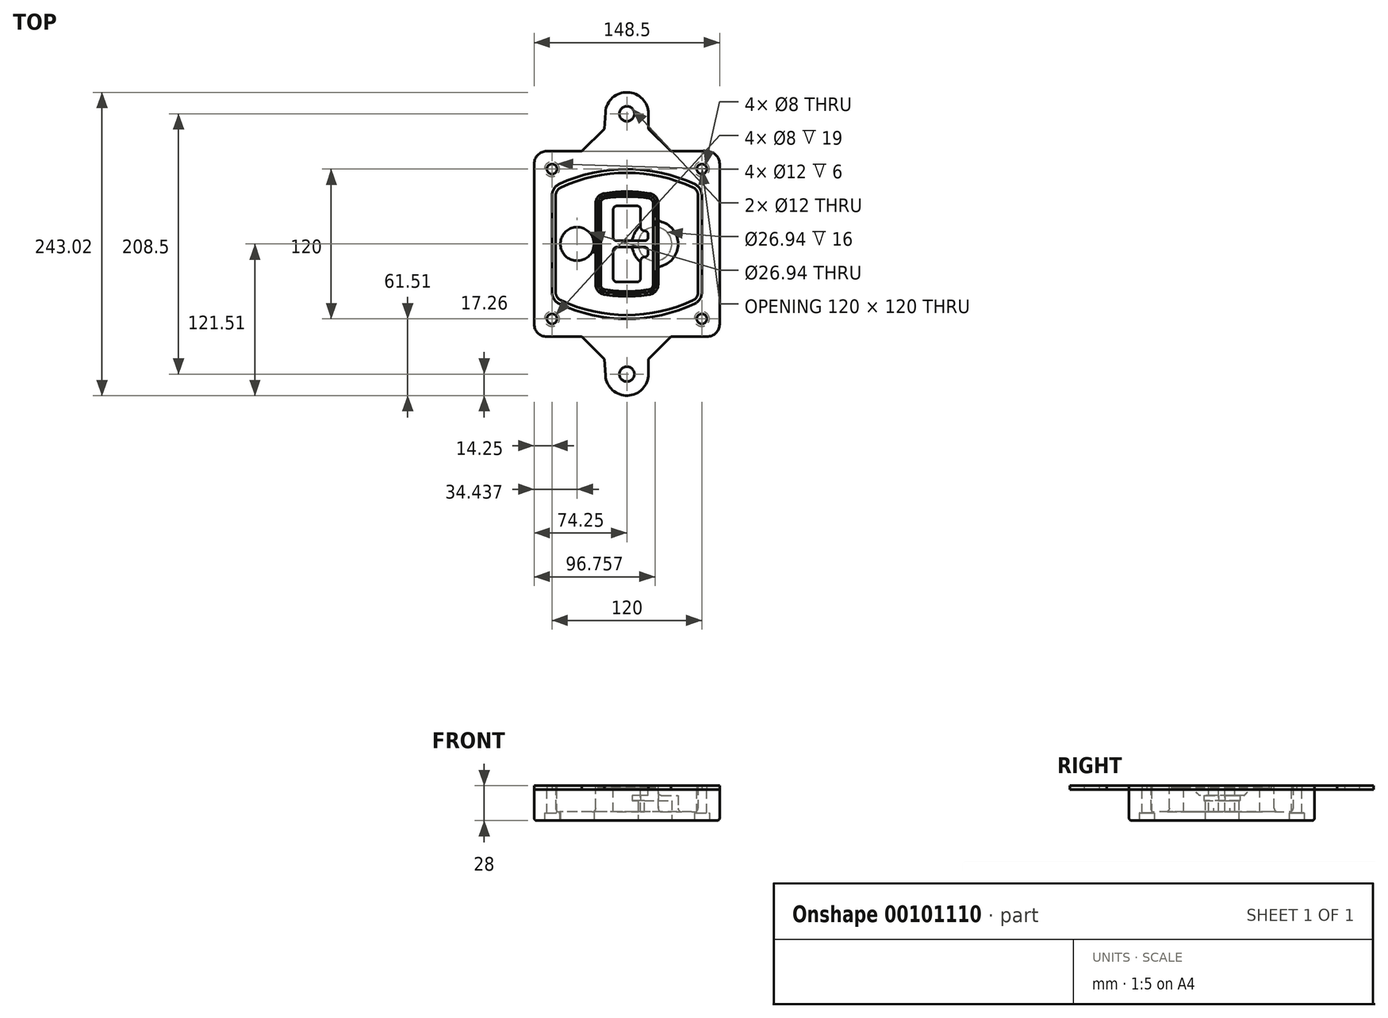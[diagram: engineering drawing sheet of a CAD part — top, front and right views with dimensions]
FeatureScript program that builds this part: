
annotation { "Feature Type Name" : "Feature", "Feature Type Description" : "" }
export const myFeature = defineFeature(function(context is Context, id is Id, definition is map)
    precondition{}
    {
        {
            var Q0;
            Q0=qCreatedBy(makeId("Top.planeOp"),FACE);
            var sketch = newSketch(context, id + "F0", { "sketchPlane" : qUnion([Q0])});
            skPoint(sketch, "E0.rect.middle", {"position": v(0, 0) * mm});
            skLineSegment(sketch, "E1.bottom", {"start": v(-64.25, -74.25) * mm, "end": v(64.25, -74.25) * mm});
            skLineSegment(sketch, "E1.top", {"start": v(-64.25, 74.25) * mm, "end": v(64.25, 74.25) * mm});
            skLineSegment(sketch, "E1.left", {"start": v(-74.25, -64.25) * mm, "end": v(-74.25, 64.25) * mm});
            skLineSegment(sketch, "E1.right", {"start": v(74.25, -64.25) * mm, "end": v(74.25, 64.25) * mm});
            skLineSegment(sketch, "E2", {"start": v(-74.25, 74.25) * mm, "end": v(74.25, -74.25) * mm, "construction": true});
            skLineSegment(sketch, "E3", {"start": v(74.25, 74.25) * mm, "end": v(-74.25, -74.25) * mm, "construction": true});
            skCircle(sketch, "E4", {"center": v(-60, 60) * mm, "radius": 4 * mm});
            skCircle(sketch, "E5", {"center": v(60, 60) * mm, "radius": 4 * mm});
            skCircle(sketch, "E6", {"center": v(60, -60) * mm, "radius": 4 * mm});
            skCircle(sketch, "E7", {"center": v(-60, -60) * mm, "radius": 4 * mm});
            skLineSegment(sketch, "E8", {"start": v(-60, 60) * mm, "end": v(60, 60) * mm, "construction": true});
            skLineSegment(sketch, "E9", {"start": v(60, 60) * mm, "end": v(60, -60) * mm, "construction": true});
            skLineSegment(sketch, "E10", {"start": v(60, -60) * mm, "end": v(-60, -60) * mm, "construction": true});
            skLineSegment(sketch, "E11", {"start": v(-60, -60) * mm, "end": v(-60, 60) * mm, "construction": true});
            skLineSegment(sketch, "E12", {"start": v(-60, 38.83) * mm, "end": v(-60, -38.83) * mm});
            skLineSegment(sketch, "E13", {"start": v(60, 38.83) * mm, "end": v(60, -38.83) * mm});
            skArc(sketch, "E14", {"start": v(54.26, 47.88) * mm, "mid": v(0, 60) * mm, "end": v(-54.26, 47.88) * mm});
            skArc(sketch, "E15", {"start": v(-54.26, -47.88) * mm, "mid": v(0, -60) * mm, "end": v(54.26, -47.88) * mm});
            skLineSegment(sketch, "E16", {"start": v(-60, 0) * mm, "end": v(60, 0) * mm, "construction": true});
            skPoint(sketch, "E17.visualSharp", {"position": v(-60, -45) * mm});
            skArc(sketch, "E17.filletArc", {"start": v(-60, -38.83) * mm, "mid": v(-58.44, -44.2) * mm, "end": v(-54.26, -47.88) * mm});
            skPoint(sketch, "E18.visualSharp", {"position": v(-60, 45) * mm});
            skArc(sketch, "E18.filletArc", {"start": v(-54.26, 47.88) * mm, "mid": v(-58.44, 44.2) * mm, "end": v(-60, 38.83) * mm});
            skPoint(sketch, "E19.visualSharp", {"position": v(60, 45) * mm});
            skArc(sketch, "E19.filletArc", {"start": v(60, 38.83) * mm, "mid": v(58.44, 44.2) * mm, "end": v(54.26, 47.88) * mm});
            skPoint(sketch, "E20.visualSharp", {"position": v(60, -45) * mm});
            skArc(sketch, "E20.filletArc", {"start": v(54.26, -47.88) * mm, "mid": v(58.44, -44.2) * mm, "end": v(60, -38.83) * mm});
            skPoint(sketch, "E21.visualSharp", {"position": v(-74.25, 74.25) * mm});
            skArc(sketch, "E21.filletArc", {"start": v(-64.25, 74.25) * mm, "mid": v(-71.32, 71.32) * mm, "end": v(-74.25, 64.25) * mm});
            skPoint(sketch, "E22.visualSharp", {"position": v(74.25, 74.25) * mm});
            skArc(sketch, "E22.filletArc", {"start": v(74.25, 64.25) * mm, "mid": v(71.32, 71.32) * mm, "end": v(64.25, 74.25) * mm});
            skPoint(sketch, "E23.visualSharp", {"position": v(74.25, -74.25) * mm});
            skArc(sketch, "E23.filletArc", {"start": v(64.25, -74.25) * mm, "mid": v(71.32, -71.32) * mm, "end": v(74.25, -64.25) * mm});
            skPoint(sketch, "E24.visualSharp", {"position": v(-74.25, -74.25) * mm});
            skArc(sketch, "E24.filletArc", {"start": v(-74.25, -64.25) * mm, "mid": v(-71.32, -71.32) * mm, "end": v(-64.25, -74.25) * mm});
            skArc(sketch, "E25.0", {"start": v(57, 38.83) * mm, "mid": v(55.9, 42.58) * mm, "end": v(52.98, 45.17) * mm});
            skLineSegment(sketch, "E25.1", {"start": v(57, 38.83) * mm, "end": v(57, -38.83) * mm});
            skArc(sketch, "E25.2", {"start": v(52.98, -45.17) * mm, "mid": v(55.9, -42.58) * mm, "end": v(57, -38.83) * mm});
            skArc(sketch, "E25.3", {"start": v(-52.98, -45.17) * mm, "mid": v(0, -57) * mm, "end": v(52.98, -45.17) * mm});
            skArc(sketch, "E25.4", {"start": v(-57, -38.83) * mm, "mid": v(-55.9, -42.58) * mm, "end": v(-52.98, -45.17) * mm});
            skArc(sketch, "E25.5", {"start": v(52.98, 45.17) * mm, "mid": v(0, 57) * mm, "end": v(-52.98, 45.17) * mm});
            skLineSegment(sketch, "E25.6", {"start": v(-57, 38.83) * mm, "end": v(-57, -38.83) * mm});
            skArc(sketch, "E25.7", {"start": v(-52.98, 45.17) * mm, "mid": v(-55.9, 42.58) * mm, "end": v(-57, 38.83) * mm});
            skArc(sketch, "E26.0", {"start": v(-55.96, 51.5) * mm, "mid": v(-61.82, 46.33) * mm, "end": v(-64, 38.83) * mm});
            skArc(sketch, "E26.1", {"start": v(55.96, 51.5) * mm, "mid": v(0, 64) * mm, "end": v(-55.96, 51.5) * mm});
            skArc(sketch, "E26.2", {"start": v(64, 38.83) * mm, "mid": v(61.82, 46.33) * mm, "end": v(55.96, 51.5) * mm});
            skLineSegment(sketch, "E26.3", {"start": v(64, 38.83) * mm, "end": v(64, -38.83) * mm});
            skArc(sketch, "E26.4", {"start": v(55.96, -51.5) * mm, "mid": v(61.82, -46.33) * mm, "end": v(64, -38.83) * mm});
            skLineSegment(sketch, "E26.5", {"start": v(-64, 38.83) * mm, "end": v(-64, -38.83) * mm});
            skArc(sketch, "E26.6", {"start": v(-55.96, -51.5) * mm, "mid": v(0, -64) * mm, "end": v(55.96, -51.5) * mm});
            skArc(sketch, "E26.7", {"start": v(-64, -38.83) * mm, "mid": v(-61.82, -46.33) * mm, "end": v(-55.96, -51.5) * mm});
            skSolve(sketch);
        }
        {
            var Q0;
            Q0=makeQuery(id+"F0.imprint","IMPRINT",FACE,{"disambiguationData":[TD([[makeQuery(id+"F0.imprint","IMPRINT",EDGE,{"derivedFrom":sQuery(id+"F0.wireOp",EDGE,"E1.bottom")}),1.0]])]});
            var Q1;
            Q1=makeQuery(id+"F0.imprint","IMPRINT",FACE,{"disambiguationData":[TD([[makeQuery(id+"F0.imprint","IMPRINT",EDGE,{"derivedFrom":sQuery(id+"F0.wireOp",EDGE,"E12")}),1.0]])]});
            var Q2;
            Q2=makeQuery(id+"F0.imprint","IMPRINT",FACE,{"disambiguationData":[TD([[makeQuery(id+"F0.imprint","IMPRINT",EDGE,{"derivedFrom":sQuery(id+"F0.wireOp",EDGE,"E25.0")}),1.0]])]});
            var Q3;
            Q3=makeQuery(id+"F0.imprint","IMPRINT",FACE,{"disambiguationData":[TD([[makeQuery(id+"F0.imprint","IMPRINT",EDGE,{"derivedFrom":sQuery(id+"F0.wireOp",EDGE,"E12")}),-1.0]])]});
            extrude(context, id + "F1", {"entities" : qUnion([Q0, Q1, Q2, Q3]), "oppositeDirection" : true, "depth" : 25 * mm});
        }
        {
            var Q0;
            Q0=makeQuery(id+"F0.imprint","IMPRINT",FACE,{"disambiguationData":[TD([[makeQuery(id+"F0.imprint","IMPRINT",EDGE,{"derivedFrom":sQuery(id+"F0.wireOp",EDGE,"E12")}),1.0]])]});
            extrude(context, id + "F2", {"entities" : qUnion([Q0]), "operationType" : NewBodyOperationType.ADD, "depth" : 3 * mm});
        }
        {
            var Q0;
            Q0=makeQuery(id+"F0.imprint","IMPRINT",FACE,{"disambiguationData":[TD([[makeQuery(id+"F0.imprint","IMPRINT",EDGE,{"derivedFrom":sQuery(id+"F0.wireOp",EDGE,"E25.0")}),1.0]])]});
            extrude(context, id + "F3", {"entities" : qUnion([Q0]), "operationType" : NewBodyOperationType.REMOVE, "oppositeDirection" : true, "depth" : 18 * mm});
        }
        {
            var Q0;
            Q0=makeQuery(id+"F2.opExtrude","CAP_FACE",FACE,{"disambiguationData":[OSD([sQuery(id+"F0.wireOp",EDGE,"E12"),sQuery(id+"F0.wireOp",EDGE,"E13"),sQuery(id+"F0.wireOp",EDGE,"E14"),sQuery(id+"F0.wireOp",EDGE,"E15"),sQuery(id+"F0.wireOp",EDGE,"E17.filletArc"),sQuery(id+"F0.wireOp",EDGE,"E18.filletArc"),sQuery(id+"F0.wireOp",EDGE,"E19.filletArc"),sQuery(id+"F0.wireOp",EDGE,"E20.filletArc"),sQuery(id+"F0.wireOp",EDGE,"E25.0"),sQuery(id+"F0.wireOp",EDGE,"E25.1"),sQuery(id+"F0.wireOp",EDGE,"E25.2"),sQuery(id+"F0.wireOp",EDGE,"E25.3"),sQuery(id+"F0.wireOp",EDGE,"E25.4"),sQuery(id+"F0.wireOp",EDGE,"E25.5"),sQuery(id+"F0.wireOp",EDGE,"E25.6"),sQuery(id+"F0.wireOp",EDGE,"E25.7")])],"isStart":false});
            var sketch = newSketch(context, id + "F4", { "sketchPlane" : qUnion([Q0])});
            skArc(sketch, "E27.0", {"start": v(-18.34, -40.45) * mm, "mid": v(0, -42) * mm, "end": v(18.34, -40.45) * mm});
            skArc(sketch, "E28.0", {"start": v(18.34, 40.45) * mm, "mid": v(0, 42) * mm, "end": v(-18.34, 40.45) * mm});
            skLineSegment(sketch, "E29", {"start": v(-25, 32.57) * mm, "end": v(-25, -32.57) * mm});
            skLineSegment(sketch, "E30", {"start": v(25, 32.57) * mm, "end": v(25, -32.57) * mm});
            skLineSegment(sketch, "E31", {"start": v(-25, 39.1) * mm, "end": v(25, 39.1) * mm, "construction": true});
            skLineSegment(sketch, "E32", {"start": v(-25, -39.1) * mm, "end": v(25, -39.1) * mm, "construction": true});
            skPoint(sketch, "E33.visualSharp", {"position": v(-25, 39.1) * mm});
            skArc(sketch, "E33.filletArc", {"start": v(-18.34, 40.45) * mm, "mid": v(-23.11, 37.73) * mm, "end": v(-25, 32.57) * mm});
            skPoint(sketch, "E34.visualSharp", {"position": v(25, 39.1) * mm});
            skArc(sketch, "E34.filletArc", {"start": v(25, 32.57) * mm, "mid": v(23.11, 37.73) * mm, "end": v(18.34, 40.45) * mm});
            skPoint(sketch, "E35.visualSharp", {"position": v(25, -39.1) * mm});
            skArc(sketch, "E35.filletArc", {"start": v(18.34, -40.45) * mm, "mid": v(23.11, -37.73) * mm, "end": v(25, -32.57) * mm});
            skPoint(sketch, "E36.visualSharp", {"position": v(-25, -39.1) * mm});
            skArc(sketch, "E36.filletArc", {"start": v(-25, -32.57) * mm, "mid": v(-23.11, -37.73) * mm, "end": v(-18.34, -40.45) * mm});
            skArc(sketch, "E37.0", {"start": v(52.98, 45.17) * mm, "mid": v(0, 57) * mm, "end": v(-52.98, 45.17) * mm});
            skArc(sketch, "E37.1", {"start": v(-52.98, 45.17) * mm, "mid": v(-55.9, 42.58) * mm, "end": v(-57, 38.83) * mm});
            skLineSegment(sketch, "E37.2", {"start": v(-57, 38.83) * mm, "end": v(-57, -38.83) * mm});
            skArc(sketch, "E37.3", {"start": v(-57, -38.83) * mm, "mid": v(-55.9, -42.58) * mm, "end": v(-52.98, -45.17) * mm});
            skArc(sketch, "E37.4", {"start": v(-52.98, -45.17) * mm, "mid": v(0, -57) * mm, "end": v(52.98, -45.17) * mm});
            skArc(sketch, "E37.5", {"start": v(52.98, -45.17) * mm, "mid": v(55.9, -42.58) * mm, "end": v(57, -38.83) * mm});
            skLineSegment(sketch, "E37.6", {"start": v(57, 38.83) * mm, "end": v(57, -38.83) * mm});
            skArc(sketch, "E37.7", {"start": v(57, 38.83) * mm, "mid": v(55.9, 42.58) * mm, "end": v(52.98, 45.17) * mm});
            skLineSegment(sketch, "E38.0", {"start": v(23, 32.57) * mm, "end": v(23, -32.57) * mm});
            skArc(sketch, "E38.1", {"start": v(18, -38.48) * mm, "mid": v(21.58, -36.44) * mm, "end": v(23, -32.57) * mm});
            skArc(sketch, "E38.2", {"start": v(-18, -38.48) * mm, "mid": v(0, -40) * mm, "end": v(18, -38.48) * mm});
            skArc(sketch, "E38.3", {"start": v(-23, -32.57) * mm, "mid": v(-21.58, -36.44) * mm, "end": v(-18, -38.48) * mm});
            skLineSegment(sketch, "E38.4", {"start": v(-23, 32.57) * mm, "end": v(-23, -32.57) * mm});
            skArc(sketch, "E38.5", {"start": v(23, 32.57) * mm, "mid": v(21.58, 36.44) * mm, "end": v(18, 38.48) * mm});
            skArc(sketch, "E38.6", {"start": v(-18, 38.48) * mm, "mid": v(-21.58, 36.44) * mm, "end": v(-23, 32.57) * mm});
            skArc(sketch, "E38.7", {"start": v(18, 38.48) * mm, "mid": v(0, 40) * mm, "end": v(-18, 38.48) * mm});
            skArc(sketch, "E39.0", {"start": v(21, 32.57) * mm, "mid": v(20.06, 35.15) * mm, "end": v(17.67, 36.5) * mm});
            skLineSegment(sketch, "E39.1", {"start": v(21, 32.57) * mm, "end": v(21, -32.57) * mm});
            skArc(sketch, "E39.2", {"start": v(17.67, -36.5) * mm, "mid": v(20.06, -35.15) * mm, "end": v(21, -32.57) * mm});
            skArc(sketch, "E39.3", {"start": v(-17.67, -36.5) * mm, "mid": v(0, -38) * mm, "end": v(17.67, -36.5) * mm});
            skArc(sketch, "E39.4", {"start": v(-21, -32.57) * mm, "mid": v(-20.06, -35.15) * mm, "end": v(-17.67, -36.5) * mm});
            skArc(sketch, "E39.5", {"start": v(17.67, 36.5) * mm, "mid": v(0, 38) * mm, "end": v(-17.67, 36.5) * mm});
            skLineSegment(sketch, "E39.6", {"start": v(-21, 32.57) * mm, "end": v(-21, -32.57) * mm});
            skArc(sketch, "E39.7", {"start": v(-17.67, 36.5) * mm, "mid": v(-20.06, 35.15) * mm, "end": v(-21, 32.57) * mm});
            skLineSegment(sketch, "E40", {"start": v(-25, 0) * mm, "end": v(25, 0) * mm, "construction": true});
            skLineSegment(sketch, "E41", {"start": v(-11, 5.5) * mm, "end": v(-11, 27.5) * mm});
            skLineSegment(sketch, "E42", {"start": v(-8, 30.5) * mm, "end": v(8, 30.5) * mm});
            skLineSegment(sketch, "E43", {"start": v(11, 27.5) * mm, "end": v(11, 13.5) * mm});
            skLineSegment(sketch, "E44", {"start": v(14, 10.5) * mm, "end": v(14, 10.5) * mm});
            skLineSegment(sketch, "E45", {"start": v(17, 7.5) * mm, "end": v(17, 5.5) * mm});
            skLineSegment(sketch, "E46", {"start": v(14, 2.5) * mm, "end": v(-8, 2.5) * mm});
            skPoint(sketch, "E47.visualSharp", {"position": v(-11, 30.5) * mm});
            skArc(sketch, "E47.filletArc", {"start": v(-8, 30.5) * mm, "mid": v(-10.12, 29.62) * mm, "end": v(-11, 27.5) * mm});
            skPoint(sketch, "E48.visualSharp", {"position": v(11, 30.5) * mm});
            skArc(sketch, "E48.filletArc", {"start": v(11, 27.5) * mm, "mid": v(10.12, 29.62) * mm, "end": v(8, 30.5) * mm});
            skPoint(sketch, "E49.visualSharp", {"position": v(11, 10.5) * mm});
            skArc(sketch, "E49.filletArc", {"start": v(11, 13.5) * mm, "mid": v(11.88, 11.38) * mm, "end": v(14, 10.5) * mm});
            skPoint(sketch, "E50.visualSharp", {"position": v(17, 10.5) * mm});
            skArc(sketch, "E50.filletArc", {"start": v(17, 7.5) * mm, "mid": v(16.12, 9.62) * mm, "end": v(14, 10.5) * mm});
            skPoint(sketch, "E51.visualSharp", {"position": v(17, 2.5) * mm});
            skArc(sketch, "E51.filletArc", {"start": v(14, 2.5) * mm, "mid": v(16.12, 3.38) * mm, "end": v(17, 5.5) * mm});
            skPoint(sketch, "E52.visualSharp", {"position": v(-11, 2.5) * mm});
            skArc(sketch, "E52.filletArc", {"start": v(-11, 5.5) * mm, "mid": v(-10.12, 3.38) * mm, "end": v(-8, 2.5) * mm});
            skLineSegment(sketch, "E53.0.MirrorCS", {"start": v(14, -2.5) * mm, "end": v(-8, -2.5) * mm});
            skArc(sketch, "E54.0.MirrorCS", {"start": v(-11, -5.5) * mm, "mid": v(-10.12, -3.38) * mm, "end": v(-8, -2.5) * mm});
            skLineSegment(sketch, "E55.0.MirrorCS", {"start": v(-11, -5.5) * mm, "end": v(-11, -27.5) * mm});
            skArc(sketch, "E56.0.MirrorCS", {"start": v(-8, -30.5) * mm, "mid": v(-10.12, -29.62) * mm, "end": v(-11, -27.5) * mm});
            skLineSegment(sketch, "E57.0.MirrorCS", {"start": v(-8, -30.5) * mm, "end": v(8, -30.5) * mm});
            skArc(sketch, "E58.0.MirrorCS", {"start": v(11, -27.5) * mm, "mid": v(10.12, -29.62) * mm, "end": v(8, -30.5) * mm});
            skLineSegment(sketch, "E59.0.MirrorCS", {"start": v(11, -27.5) * mm, "end": v(11, -13.5) * mm});
            skArc(sketch, "E60.0.MirrorCS", {"start": v(11, -13.5) * mm, "mid": v(11.88, -11.38) * mm, "end": v(14, -10.5) * mm});
            skArc(sketch, "E61.0.MirrorCS", {"start": v(17, -7.5) * mm, "mid": v(16.12, -9.62) * mm, "end": v(14, -10.5) * mm});
            skLineSegment(sketch, "E62.0.MirrorCS", {"start": v(17, -7.5) * mm, "end": v(17, -5.5) * mm});
            skArc(sketch, "E63.0.MirrorCS", {"start": v(14, -2.5) * mm, "mid": v(16.12, -3.38) * mm, "end": v(17, -5.5) * mm});
            skSolve(sketch);
        }
        {
            var Q0;
            Q0=makeQuery(id+"F4.imprint","IMPRINT",FACE,{"disambiguationData":[TD([[makeQuery(id+"F4.imprint","IMPRINT",EDGE,{"derivedFrom":sQuery(id+"F4.wireOp",EDGE,"E27.0")}),1.0]])]});
            var Q1;
            Q1=makeQuery(id+"F4.imprint","IMPRINT",FACE,{"disambiguationData":[TD([[makeQuery(id+"F4.imprint","IMPRINT",EDGE,{"derivedFrom":sQuery(id+"F4.wireOp",EDGE,"E38.0")}),-1.0]])]});
            var Q2;
            Q2=makeQuery(id+"F4.imprint","IMPRINT",FACE,{"disambiguationData":[TD([[makeQuery(id+"F4.imprint","IMPRINT",EDGE,{"derivedFrom":sQuery(id+"F4.wireOp",EDGE,"E39.0")}),1.0]])]});
            extrude(context, id + "F5", {"entities" : qUnion([Q0, Q1, Q2]), "operationType" : NewBodyOperationType.ADD, "endBound" : BoundingType.UP_TO_NEXT, "oppositeDirection" : true, "depth" : 25 * mm});
        }
        {
            var Q0;
            Q0=makeQuery(id+"F4.imprint","IMPRINT",FACE,{"disambiguationData":[TD([[makeQuery(id+"F4.imprint","IMPRINT",EDGE,{"derivedFrom":sQuery(id+"F4.wireOp",EDGE,"E38.0")}),-1.0]])]});
            extrude(context, id + "F6", {"entities" : qUnion([Q0]), "operationType" : NewBodyOperationType.REMOVE, "oppositeDirection" : true, "depth" : 2 * mm});
        }
        {
            var Q0;
            Q0=makeQuery(id+"F1.opExtrude","CAP_FACE",FACE,{"disambiguationData":[OSD([sQuery(id+"F0.wireOp",EDGE,"E1.bottom"),sQuery(id+"F0.wireOp",EDGE,"E1.top"),sQuery(id+"F0.wireOp",EDGE,"E1.left"),sQuery(id+"F0.wireOp",EDGE,"E1.right"),sQuery(id+"F0.wireOp",EDGE,"E4"),sQuery(id+"F0.wireOp",EDGE,"E5"),sQuery(id+"F0.wireOp",EDGE,"E6"),sQuery(id+"F0.wireOp",EDGE,"E7"),sQuery(id+"F0.wireOp",EDGE,"E21.filletArc"),sQuery(id+"F0.wireOp",EDGE,"E22.filletArc"),sQuery(id+"F0.wireOp",EDGE,"E23.filletArc"),sQuery(id+"F0.wireOp",EDGE,"E24.filletArc")])],"isStart":false});
            var sketch = newSketch(context, id + "F7", { "sketchPlane" : qUnion([Q0])});
            skCircle(sketch, "E64", {"center": v(22.5, 0) * mm, "radius": 13.47 * mm});
            skCircle(sketch, "E65", {"center": v(-39.81, 0) * mm, "radius": 13.47 * mm});
            skLineSegment(sketch, "E66", {"start": v(74.25, 0) * mm, "end": v(-74.25, 0) * mm});
            skCircle(sketch, "E67", {"center": v(22.5, 0) * mm, "radius": 18.47 * mm});
            skCircle(sketch, "E68", {"center": v(60, -60) * mm, "radius": 6 * mm});
            skCircle(sketch, "E69", {"center": v(-60, -60) * mm, "radius": 6 * mm});
            skCircle(sketch, "E70", {"center": v(-60, 60) * mm, "radius": 6 * mm});
            skCircle(sketch, "E71", {"center": v(60, 60) * mm, "radius": 6 * mm});
            skSolve(sketch);
        }
        {
            var Q0;
            {var subQ1=sQuery(id+"F7.wireOp",EDGE,"E66");var subQ4=sQuery(id+"F7.wireOp",EDGE,"E64");var subQ6=makeQuery(id+"F7.imprint","INTERSECT",VERTEX,{"disambiguationData":[OD(0.0)],"derivedFrom":[subQ4,subQ1]});Q0=makeQuery(id+"F7.imprint","IMPRINT",FACE,{"disambiguationData":[TD([[makeQuery(id+"F7.imprint","IMPRINT",EDGE,{"disambiguationData":[TD([[subQ6,-1.0]])],"derivedFrom":subQ4}),-1.0]])]});}
            var Q1;
            {var subQ0=sQuery(id+"F7.wireOp",EDGE,"E66");var subQ1=sQuery(id+"F7.wireOp",EDGE,"E64");var subQ3=makeQuery(id+"F7.imprint","INTERSECT",VERTEX,{"disambiguationData":[OD(0.0)],"derivedFrom":[subQ1,subQ0]});Q1=makeQuery(id+"F7.imprint","IMPRINT",FACE,{"disambiguationData":[TD([[makeQuery(id+"F7.imprint","IMPRINT",EDGE,{"disambiguationData":[TD([[subQ3,-1.0]])],"derivedFrom":subQ1}),1.0]])]});}
            var Q2;
            {var subQ0=sQuery(id+"F7.wireOp",EDGE,"E66");var subQ1=sQuery(id+"F7.wireOp",EDGE,"E64");var subQ3=makeQuery(id+"F7.imprint","INTERSECT",VERTEX,{"disambiguationData":[OD(0.0)],"derivedFrom":[subQ1,subQ0]});Q2=makeQuery(id+"F7.imprint","IMPRINT",FACE,{"disambiguationData":[TD([[makeQuery(id+"F7.imprint","IMPRINT",EDGE,{"disambiguationData":[TD([[subQ3,1.0]])],"derivedFrom":subQ1}),1.0]])]});}
            var Q3;
            {var subQ1=sQuery(id+"F7.wireOp",EDGE,"E66");var subQ4=sQuery(id+"F7.wireOp",EDGE,"E64");var subQ6=makeQuery(id+"F7.imprint","INTERSECT",VERTEX,{"disambiguationData":[OD(0.0)],"derivedFrom":[subQ4,subQ1]});Q3=makeQuery(id+"F7.imprint","IMPRINT",FACE,{"disambiguationData":[TD([[makeQuery(id+"F7.imprint","IMPRINT",EDGE,{"disambiguationData":[TD([[subQ6,1.0]])],"derivedFrom":subQ4}),-1.0]])]});}
            extrude(context, id + "F8", {"entities" : qUnion([Q0, Q1, Q2, Q3]), "operationType" : NewBodyOperationType.ADD, "oppositeDirection" : true, "depth" : 20 * mm});
        }
        {
            var Q0;
            {var subQ0=sQuery(id+"F7.wireOp",EDGE,"E66");var subQ1=sQuery(id+"F7.wireOp",EDGE,"E64");var subQ3=makeQuery(id+"F7.imprint","INTERSECT",VERTEX,{"disambiguationData":[OD(0.0)],"derivedFrom":[subQ1,subQ0]});Q0=makeQuery(id+"F7.imprint","IMPRINT",FACE,{"disambiguationData":[TD([[makeQuery(id+"F7.imprint","IMPRINT",EDGE,{"disambiguationData":[TD([[subQ3,-1.0]])],"derivedFrom":subQ1}),1.0]])]});}
            var Q1;
            {var subQ0=sQuery(id+"F7.wireOp",EDGE,"E66");var subQ1=sQuery(id+"F7.wireOp",EDGE,"E64");var subQ3=makeQuery(id+"F7.imprint","INTERSECT",VERTEX,{"disambiguationData":[OD(0.0)],"derivedFrom":[subQ1,subQ0]});Q1=makeQuery(id+"F7.imprint","IMPRINT",FACE,{"disambiguationData":[TD([[makeQuery(id+"F7.imprint","IMPRINT",EDGE,{"disambiguationData":[TD([[subQ3,1.0]])],"derivedFrom":subQ1}),1.0]])]});}
            extrude(context, id + "F9", {"entities" : qUnion([Q0, Q1]), "operationType" : NewBodyOperationType.REMOVE, "oppositeDirection" : true, "depth" : 16 * mm});
        }
        {
            var Q0;
            {var subQ0=sQuery(id+"F7.wireOp",EDGE,"E66");var subQ1=sQuery(id+"F7.wireOp",EDGE,"E65");var subQ3=makeQuery(id+"F7.imprint","INTERSECT",VERTEX,{"disambiguationData":[OD(0.0)],"derivedFrom":[subQ1,subQ0]});Q0=makeQuery(id+"F7.imprint","IMPRINT",FACE,{"disambiguationData":[TD([[makeQuery(id+"F7.imprint","IMPRINT",EDGE,{"disambiguationData":[TD([[subQ3,-1.0]])],"derivedFrom":subQ1}),1.0]])]});}
            var Q1;
            {var subQ0=sQuery(id+"F7.wireOp",EDGE,"E66");var subQ1=sQuery(id+"F7.wireOp",EDGE,"E65");var subQ3=makeQuery(id+"F7.imprint","INTERSECT",VERTEX,{"disambiguationData":[OD(0.0)],"derivedFrom":[subQ1,subQ0]});Q1=makeQuery(id+"F7.imprint","IMPRINT",FACE,{"disambiguationData":[TD([[makeQuery(id+"F7.imprint","IMPRINT",EDGE,{"disambiguationData":[TD([[subQ3,1.0]])],"derivedFrom":subQ1}),1.0]])]});}
            extrude(context, id + "F10", {"entities" : qUnion([Q0, Q1]), "operationType" : NewBodyOperationType.REMOVE, "oppositeDirection" : true, "depth" : 25 * mm});
        }
        {
            var Q0;
            Q0=makeQuery(id+"F7.imprint","IMPRINT",FACE,{"disambiguationData":[TD([[makeQuery(id+"F7.imprint","IMPRINT",EDGE,{"derivedFrom":sQuery(id+"F7.wireOp",EDGE,"E68")}),1.0]])]});
            var Q1;
            Q1=makeQuery(id+"F7.imprint","IMPRINT",FACE,{"disambiguationData":[TD([[makeQuery(id+"F7.imprint","IMPRINT",EDGE,{"derivedFrom":makeQuery(id+"F1.opExtrude","CAP_EDGE",EDGE,{"disambiguationData":[OSD([sQuery(id+"F0.wireOp",EDGE,"E5")])],"isStart":false})}),-1.0]])]});
            var Q2;
            Q2=makeQuery(id+"F7.imprint","IMPRINT",FACE,{"disambiguationData":[TD([[makeQuery(id+"F7.imprint","IMPRINT",EDGE,{"derivedFrom":sQuery(id+"F7.wireOp",EDGE,"E69")}),1.0]])]});
            var Q3;
            Q3=makeQuery(id+"F7.imprint","IMPRINT",FACE,{"disambiguationData":[TD([[makeQuery(id+"F7.imprint","IMPRINT",EDGE,{"derivedFrom":makeQuery(id+"F1.opExtrude","CAP_EDGE",EDGE,{"disambiguationData":[OSD([sQuery(id+"F0.wireOp",EDGE,"E4")])],"isStart":false})}),-1.0]])]});
            var Q4;
            Q4=makeQuery(id+"F7.imprint","IMPRINT",FACE,{"disambiguationData":[TD([[makeQuery(id+"F7.imprint","IMPRINT",EDGE,{"derivedFrom":sQuery(id+"F7.wireOp",EDGE,"E70")}),1.0]])]});
            var Q5;
            Q5=makeQuery(id+"F7.imprint","IMPRINT",FACE,{"disambiguationData":[TD([[makeQuery(id+"F7.imprint","IMPRINT",EDGE,{"derivedFrom":makeQuery(id+"F1.opExtrude","CAP_EDGE",EDGE,{"disambiguationData":[OSD([sQuery(id+"F0.wireOp",EDGE,"E7")])],"isStart":false})}),-1.0]])]});
            var Q6;
            Q6=makeQuery(id+"F7.imprint","IMPRINT",FACE,{"disambiguationData":[TD([[makeQuery(id+"F7.imprint","IMPRINT",EDGE,{"derivedFrom":sQuery(id+"F7.wireOp",EDGE,"E71")}),1.0]])]});
            var Q7;
            Q7=makeQuery(id+"F7.imprint","IMPRINT",FACE,{"disambiguationData":[TD([[makeQuery(id+"F7.imprint","IMPRINT",EDGE,{"derivedFrom":makeQuery(id+"F1.opExtrude","CAP_EDGE",EDGE,{"disambiguationData":[OSD([sQuery(id+"F0.wireOp",EDGE,"E6")])],"isStart":false})}),-1.0]])]});
            extrude(context, id + "F11", {"entities" : qUnion([Q0, Q1, Q2, Q3, Q4, Q5, Q6, Q7]), "operationType" : NewBodyOperationType.REMOVE, "oppositeDirection" : true, "depth" : 6 * mm});
        }
        {
            var Q0;
            Q0=makeQuery(id+"F9.boolean.opBoolean","COPY",FACE,{"derivedFrom":makeQuery(id+"F9.opExtrude","CAP_FACE",FACE,{"disambiguationData":[OSD([sQuery(id+"F7.wireOp",EDGE,"E64")])],"isStart":false})});
            var sketch = newSketch(context, id + "F12", { "sketchPlane" : qUnion([Q0])});
            skArc(sketch, "E72.0", {"start": v(11, 14.45) * mm, "mid": v(6.45, 9.13) * mm, "end": v(4.2, 2.5) * mm});
            skArc(sketch, "E72.1", {"start": v(4.2, -2.5) * mm, "mid": v(6.45, -9.13) * mm, "end": v(11, -14.45) * mm});
            skLineSegment(sketch, "E73", {"start": v(4.2, -2.5) * mm, "end": v(14, -2.5) * mm});
            skLineSegment(sketch, "E74.0", {"start": v(14, 2.5) * mm, "end": v(4.2, 2.5) * mm});
            skArc(sketch, "E74.1", {"start": v(14, 2.5) * mm, "mid": v(16.12, 3.38) * mm, "end": v(17, 5.5) * mm});
            skLineSegment(sketch, "E74.2", {"start": v(17, 7.5) * mm, "end": v(17, 5.5) * mm});
            skArc(sketch, "E74.3", {"start": v(17, 7.5) * mm, "mid": v(16.12, 9.62) * mm, "end": v(14, 10.5) * mm});
            skArc(sketch, "E74.4", {"start": v(11, 13.5) * mm, "mid": v(11.88, 11.38) * mm, "end": v(14, 10.5) * mm});
            skLineSegment(sketch, "E74.5", {"start": v(11, 14.45) * mm, "end": v(11, 13.5) * mm});
            skLineSegment(sketch, "E74.7", {"start": v(14, -2.5) * mm, "end": v(4.2, -2.5) * mm});
            skArc(sketch, "E74.8", {"start": v(14, -2.5) * mm, "mid": v(16.12, -3.38) * mm, "end": v(17, -5.5) * mm});
            skLineSegment(sketch, "E74.9", {"start": v(17, -7.5) * mm, "end": v(17, -5.5) * mm});
            skArc(sketch, "E74.10", {"start": v(17, -7.5) * mm, "mid": v(16.12, -9.62) * mm, "end": v(14, -10.5) * mm});
            skArc(sketch, "E74.11", {"start": v(11, -13.5) * mm, "mid": v(11.88, -11.38) * mm, "end": v(14, -10.5) * mm});
            skLineSegment(sketch, "E74.12", {"start": v(11, -14.45) * mm, "end": v(11, -13.5) * mm});
            skPoint(sketch, "E75.orphan", {"position": v(11, -27.5) * mm});
            skPoint(sketch, "E76.orphan", {"position": v(-8, -2.5) * mm});
            skPoint(sketch, "E77.orphan", {"position": v(-8, 2.5) * mm});
            skPoint(sketch, "E78.orphan", {"position": v(11, 27.5) * mm});
            skSolve(sketch);
        }
        {
            var Q0;
            {var subQ7=sQuery(id+"F12.wireOp",EDGE,"E72.0");var subQ14=sQuery(id+"F12.wireOp",EDGE,"E72.1");var subQ16=sQuery(id+"F12.wireOp",EDGE,"E74.1");var subQ18=sQuery(id+"F12.wireOp",EDGE,"E74.8");Q0=qUnion([makeQuery(id+"F12.imprint","IMPRINT",FACE,{"disambiguationData":[TD([[makeQuery(id+"F12.imprint","IMPRINT",EDGE,{"derivedFrom":subQ7}),1.0]])]}),makeQuery(id+"F12.imprint","IMPRINT",FACE,{"disambiguationData":[TD([[makeQuery(id+"F12.imprint","IMPRINT",EDGE,{"derivedFrom":subQ14}),1.0]])]}),makeQuery(id+"F12.imprint","IMPRINT",FACE,{"disambiguationData":[TD([[makeQuery(id+"F12.imprint","IMPRINT",EDGE,{"derivedFrom":subQ16}),1.0]])]}),makeQuery(id+"F12.imprint","IMPRINT",FACE,{"disambiguationData":[TD([[makeQuery(id+"F12.imprint","IMPRINT",EDGE,{"derivedFrom":subQ18}),-1.0]])]})]);}
            var Q1;
            Q1=makeQuery(id+"F5.boolean.opBoolean","SPLIT",FACE,{"disambiguationData":[TD([makeQuery(id+"F5.opExtrude","SWEPT_FACE",FACE,{"disambiguationData":[OSD([sQuery(id+"F4.wireOp",EDGE,"E41")])]})])],"derivedFrom":makeQuery(id+"F3.boolean.opBoolean","COPY",FACE,{"derivedFrom":makeQuery(id+"F3.opExtrude","CAP_FACE",FACE,{"disambiguationData":[OSD([sQuery(id+"F0.wireOp",EDGE,"E25.0"),sQuery(id+"F0.wireOp",EDGE,"E25.1"),sQuery(id+"F0.wireOp",EDGE,"E25.2"),sQuery(id+"F0.wireOp",EDGE,"E25.3"),sQuery(id+"F0.wireOp",EDGE,"E25.4"),sQuery(id+"F0.wireOp",EDGE,"E25.5"),sQuery(id+"F0.wireOp",EDGE,"E25.6"),sQuery(id+"F0.wireOp",EDGE,"E25.7")])],"isStart":false})})});
            extrude(context, id + "F13", {"entities" : qUnion([Q0]), "operationType" : NewBodyOperationType.REMOVE, "endBound" : BoundingType.UP_TO_SURFACE, "endBoundEntityFace" : qUnion([Q1]), "depth" : 25 * mm});
        }
        {
            var Q0;
            Q0=makeQuery(id+"F3.boolean.opBoolean","COPY",EDGE,{"derivedFrom":makeQuery(id+"F3.opExtrude","CAP_EDGE",EDGE,{"disambiguationData":[OSD([sQuery(id+"F0.wireOp",EDGE,"E25.6")])],"isStart":false})});
            var Q1;
            Q1=makeQuery(id+"F8.boolean.opBoolean","INTERSECT",EDGE,{"derivedFrom":[makeQuery(id+"F5.opExtrude","SWEPT_FACE",FACE,{"disambiguationData":[OSD([sQuery(id+"F4.wireOp",EDGE,"E30")])]}),makeQuery(id+"F8.opExtrude","CAP_FACE",FACE,{"disambiguationData":[OSD([sQuery(id+"F7.wireOp",EDGE,"E67")])],"isStart":false})]});
            var Q2;
            Q2=makeQuery(id+"F8.boolean.opBoolean","INTERSECT",EDGE,{"disambiguationData":[OD(1.0)],"derivedFrom":[makeQuery(id+"F5.opExtrude","SWEPT_FACE",FACE,{"disambiguationData":[OSD([sQuery(id+"F4.wireOp",EDGE,"E30")])]}),makeQuery(id+"F8.opExtrude","SWEPT_FACE",FACE,{"disambiguationData":[OSD([sQuery(id+"F7.wireOp",EDGE,"E67")])]})]});
            var Q3;
            {var subQ0=sQuery(id+"F4.wireOp",EDGE,"E30");Q3=makeQuery(id+"F8.boolean.opBoolean","SPLIT",EDGE,{"disambiguationData":[TD([makeQuery(id+"F5.opExtrude","SWEPT_FACE",FACE,{"disambiguationData":[OSD([sQuery(id+"F4.wireOp",EDGE,"E35.filletArc")])]})])],"derivedFrom":makeQuery(id+"F5.opExtrude","CAP_EDGE",EDGE,{"disambiguationData":[OSD([subQ0])],"isStart":false})});}
            var Q4;
            {var subQ0=sQuery(id+"F0.wireOp",EDGE,"E25.7");var subQ1=sQuery(id+"F0.wireOp",EDGE,"E25.1");var subQ2=sQuery(id+"F0.wireOp",EDGE,"E25.6");var subQ3=sQuery(id+"F0.wireOp",EDGE,"E25.5");var subQ4=sQuery(id+"F0.wireOp",EDGE,"E25.4");var subQ5=sQuery(id+"F0.wireOp",EDGE,"E25.0");var subQ6=sQuery(id+"F0.wireOp",EDGE,"E25.2");var subQ7=sQuery(id+"F0.wireOp",EDGE,"E25.3");Q4=makeQuery(id+"F8.boolean.opBoolean","INTERSECT",EDGE,{"derivedFrom":[makeQuery(id+"F5.boolean.opBoolean","SPLIT",FACE,{"disambiguationData":[TD([makeQuery(id+"F2.opExtrude","SWEPT_FACE",FACE,{"disambiguationData":[OSD([subQ5])]})])],"derivedFrom":makeQuery(id+"F3.boolean.opBoolean","COPY",FACE,{"derivedFrom":makeQuery(id+"F3.opExtrude","CAP_FACE",FACE,{"disambiguationData":[OSD([subQ5,subQ1,subQ6,subQ7,subQ4,subQ3,subQ2,subQ0])],"isStart":false})})}),makeQuery(id+"F8.opExtrude","SWEPT_FACE",FACE,{"disambiguationData":[OSD([sQuery(id+"F7.wireOp",EDGE,"E67")])]})]});}
            var Q5;
            Q5=makeQuery(id+"F8.boolean.opBoolean","INTERSECT",EDGE,{"disambiguationData":[OD(0.0)],"derivedFrom":[makeQuery(id+"F5.opExtrude","SWEPT_FACE",FACE,{"disambiguationData":[OSD([sQuery(id+"F4.wireOp",EDGE,"E30")])]}),makeQuery(id+"F8.opExtrude","SWEPT_FACE",FACE,{"disambiguationData":[OSD([sQuery(id+"F7.wireOp",EDGE,"E67")])]})]});
            fillet(context, id + "F14", {"entities" : qUnion([Q0, Q1, Q2, Q3, Q4, Q5]), "radius" : 3 * mm, "tangentPropagation" : true, "allowEdgeOverflow" : false});
        }
        {
            var Q0;
            Q0=makeQuery(id+"F1.opExtrude","CAP_EDGE",EDGE,{"disambiguationData":[OSD([sQuery(id+"F0.wireOp",EDGE,"E1.bottom")])],"isStart":false});
            fillet(context, id + "F15", {"entities" : qUnion([Q0]), "radius" : 2 * mm, "tangentPropagation" : true, "allowEdgeOverflow" : false});
        }
        {
            var Q0;
            {var subQ0=sQuery(id+"F0.wireOp",EDGE,"E22.filletArc");var subQ1=sQuery(id+"F0.wireOp",EDGE,"E7");var subQ2=sQuery(id+"F0.wireOp",EDGE,"E6");var subQ3=sQuery(id+"F0.wireOp",EDGE,"E5");var subQ4=sQuery(id+"F0.wireOp",EDGE,"E4");var subQ5=sQuery(id+"F0.wireOp",EDGE,"E1.bottom");var subQ6=sQuery(id+"F0.wireOp",EDGE,"E21.filletArc");var subQ7=sQuery(id+"F0.wireOp",EDGE,"E1.top");var subQ8=sQuery(id+"F0.wireOp",EDGE,"E1.left");var subQ9=sQuery(id+"F0.wireOp",EDGE,"E1.right");var subQ10=sQuery(id+"F0.wireOp",EDGE,"E23.filletArc");var subQ11=sQuery(id+"F0.wireOp",EDGE,"E24.filletArc");Q0=makeQuery(id+"F2.boolean.opBoolean","SPLIT",FACE,{"disambiguationData":[TD([makeQuery(id+"F1.opExtrude","SWEPT_FACE",FACE,{"disambiguationData":[OSD([subQ5])]})])],"derivedFrom":makeQuery(id+"F1.opExtrude","CAP_FACE",FACE,{"disambiguationData":[OSD([subQ5,subQ7,subQ8,subQ9,subQ4,subQ3,subQ2,subQ1,subQ6,subQ0,subQ10,subQ11])],"isStart":true})});}
            var sketch = newSketch(context, id + "F16", { "sketchPlane" : qUnion([Q0])});
            skCircle(sketch, "E79", {"center": v(0, -104.25) * mm, "radius": 6 * mm});
            skPoint(sketch, "E79.centerSnap0", {"position": v(0, -74.25) * mm});
            skLineSegment(sketch, "E80", {"start": v(0, -74.25) * mm, "end": v(0, -104.25) * mm, "construction": true});
            skLineSegment(sketch, "E81", {"start": v(35.26, -74.25) * mm, "end": v(17.26, -92.25) * mm});
            skLineSegment(sketch, "E82", {"start": v(35.26, -74.25) * mm, "end": v(0, -74.25) * mm});
            skLineSegment(sketch, "E83", {"start": v(-18.14, -92.25) * mm, "end": v(-36.14, -74.25) * mm});
            skLineSegment(sketch, "E84", {"start": v(17.26, -92.25) * mm, "end": v(17.26, -104.25) * mm});
            skLineSegment(sketch, "E85", {"start": v(-17.21, -105.46) * mm, "end": v(-18.14, -92.25) * mm});
            skArc(sketch, "E86", {"start": v(-17.21, -105.46) * mm, "mid": v(0.6, -121.5) * mm, "end": v(17.26, -104.25) * mm});
            skPoint(sketch, "E87.endSnap0", {"position": v(0, 74.25) * mm});
            skLineSegment(sketch, "E88", {"start": v(-74.25, 0) * mm, "end": v(74.25, 0) * mm});
            skLineSegment(sketch, "E89.MirrorCS", {"start": v(-18.14, 92.25) * mm, "end": v(-36.14, 74.25) * mm});
            skLineSegment(sketch, "E90.MirrorCS", {"start": v(-17.21, 105.46) * mm, "end": v(-18.14, 92.25) * mm});
            skArc(sketch, "E91.MirrorCS", {"start": v(-17.21, 105.46) * mm, "mid": v(0.6, 121.5) * mm, "end": v(17.26, 104.25) * mm});
            skLineSegment(sketch, "E92.MirrorCS", {"start": v(17.26, 92.25) * mm, "end": v(17.26, 104.25) * mm});
            skLineSegment(sketch, "E93.MirrorCS", {"start": v(35.26, 74.25) * mm, "end": v(17.26, 92.25) * mm});
            skCircle(sketch, "E94.MirrorC", {"center": v(0, 104.25) * mm, "radius": 6 * mm});
            skLineSegment(sketch, "E95.MirrorCS", {"start": v(0, 74.25) * mm, "end": v(0, 104.25) * mm, "construction": true});
            skSolve(sketch);
        }
        {
            var Q0;
            Q0=makeQuery(id+"F16.imprint","IMPRINT",FACE,{"disambiguationData":[TD([[makeQuery(id+"F16.imprint","IMPRINT",EDGE,{"derivedFrom":sQuery(id+"F16.wireOp",EDGE,"E79")}),-1.0]])]});
            var Q1;
            {var subQ11=sQuery(id+"F16.wireOp",EDGE,"E82");Q1=makeQuery(id+"F16.imprint","IMPRINT",FACE,{"disambiguationData":[TD([[makeQuery(id+"F16.imprint","IMPRINT",EDGE,{"derivedFrom":subQ11}),1.0]])]});}
            var Q2;
            Q2=makeQuery(id+"F16.imprint","IMPRINT",FACE,{"disambiguationData":[TD([[makeQuery(id+"F16.imprint","IMPRINT",EDGE,{"derivedFrom":makeQuery(id+"F1.opExtrude","CAP_EDGE",EDGE,{"disambiguationData":[OSD([sQuery(id+"F0.wireOp",EDGE,"E4")])],"isStart":true})}),-1.0]])]});
            var Q3;
            {var subQ0=sQuery(id+"F16.wireOp",EDGE,"E89.MirrorCS");Q3=makeQuery(id+"F16.imprint","IMPRINT",FACE,{"disambiguationData":[TD([[makeQuery(id+"F16.imprint","IMPRINT",EDGE,{"derivedFrom":subQ0}),1.0]])]});}
            var Q4;
            Q4=makeQuery(id+"F2.opExtrude","CAP_FACE",FACE,{"disambiguationData":[OSD([sQuery(id+"F0.wireOp",EDGE,"E12"),sQuery(id+"F0.wireOp",EDGE,"E13"),sQuery(id+"F0.wireOp",EDGE,"E14"),sQuery(id+"F0.wireOp",EDGE,"E15"),sQuery(id+"F0.wireOp",EDGE,"E17.filletArc"),sQuery(id+"F0.wireOp",EDGE,"E18.filletArc"),sQuery(id+"F0.wireOp",EDGE,"E19.filletArc"),sQuery(id+"F0.wireOp",EDGE,"E20.filletArc"),sQuery(id+"F0.wireOp",EDGE,"E25.0"),sQuery(id+"F0.wireOp",EDGE,"E25.1"),sQuery(id+"F0.wireOp",EDGE,"E25.2"),sQuery(id+"F0.wireOp",EDGE,"E25.3"),sQuery(id+"F0.wireOp",EDGE,"E25.4"),sQuery(id+"F0.wireOp",EDGE,"E25.5"),sQuery(id+"F0.wireOp",EDGE,"E25.6"),sQuery(id+"F0.wireOp",EDGE,"E25.7")])],"isStart":false});
            extrude(context, id + "F17", {"entities" : qUnion([Q0, Q1, Q2, Q3]), "endBound" : BoundingType.UP_TO_SURFACE, "endBoundEntityFace" : qUnion([Q4]), "depth" : 25 * mm});
        }
    });
